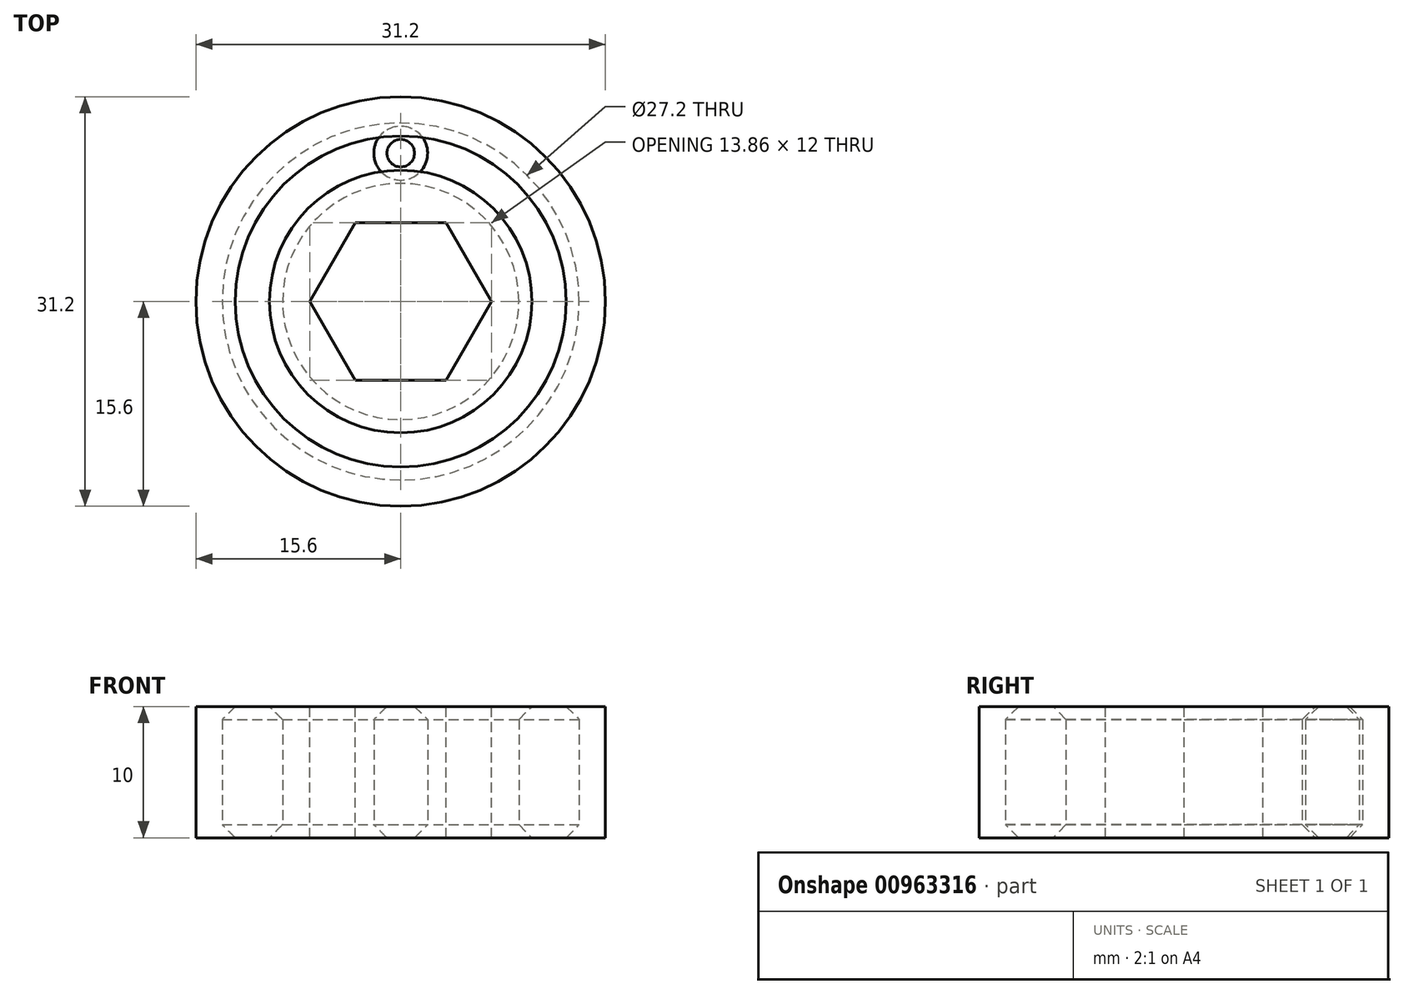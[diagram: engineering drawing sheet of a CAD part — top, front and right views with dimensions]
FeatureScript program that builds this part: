
annotation { "Feature Type Name" : "Feature", "Feature Type Description" : "" }
export const myFeature = defineFeature(function(context is Context, id is Id, definition is map)
    precondition{}
    {
        {
            var Q0;
            Q0=qCreatedBy(makeId("Right.planeOp"),FACE);
            var sketch = newSketch(context, id + "F0", { "sketchPlane" : qUnion([Q0])});
            skLineSegment(sketch, "E0", {"start": v(0, 0) * mm, "end": v(0, 10) * mm});
            skLineSegment(sketch, "E1", {"start": v(0, 0) * mm, "end": v(10, 0) * mm});
            skLineSegment(sketch, "E2", {"start": v(10, 0) * mm, "end": v(9, 1) * mm});
            skLineSegment(sketch, "E3", {"start": v(9, 1) * mm, "end": v(9, 9) * mm});
            skLineSegment(sketch, "E4", {"start": v(9, 9) * mm, "end": v(10, 10) * mm});
            skLineSegment(sketch, "E5", {"start": v(10, 10) * mm, "end": v(0, 10) * mm});
            skLineSegment(sketch, "E6", {"start": v(9.25, 1) * mm, "end": v(9.25, 9) * mm});
            skLineSegment(sketch, "E7", {"start": v(9.25, 9) * mm, "end": v(10.25, 10) * mm});
            skLineSegment(sketch, "E8", {"start": v(9.25, 1) * mm, "end": v(10.25, 0) * mm});
            skLineSegment(sketch, "E9", {"start": v(10.25, 10) * mm, "end": v(11.3, 10) * mm});
            skLineSegment(sketch, "E10", {"start": v(10.25, 0) * mm, "end": v(11.3, 0) * mm});
            skLineSegment(sketch, "E11", {"start": v(11.3, 0) * mm, "end": v(11.3, 10) * mm});
            skLineSegment(sketch, "E12.MirrorCS", {"start": v(13.35, 1) * mm, "end": v(13.35, 9) * mm});
            skLineSegment(sketch, "E13.MirrorCS", {"start": v(13.35, 9) * mm, "end": v(12.35, 10) * mm});
            skLineSegment(sketch, "E14.MirrorCS", {"start": v(13.35, 1) * mm, "end": v(12.35, 0) * mm});
            skLineSegment(sketch, "E15.MirrorCS", {"start": v(12.6, 10) * mm, "end": v(15.6, 10) * mm});
            skLineSegment(sketch, "E16.MirrorCS", {"start": v(13.6, 9) * mm, "end": v(12.6, 10) * mm});
            skLineSegment(sketch, "E17.MirrorCS", {"start": v(13.6, 1) * mm, "end": v(13.6, 9) * mm});
            skLineSegment(sketch, "E18.MirrorCS", {"start": v(12.6, 0) * mm, "end": v(13.6, 1) * mm});
            skLineSegment(sketch, "E19.MirrorCS", {"start": v(15.6, 0) * mm, "end": v(12.6, 0) * mm});
            skLineSegment(sketch, "E20", {"start": v(15.6, 10) * mm, "end": v(15.6, 0) * mm});
            skPoint(sketch, "E21.orphan", {"position": v(22.6, 10) * mm});
            skPoint(sketch, "E22.orphan", {"position": v(22.6, 0) * mm});
            skSolve(sketch);
        }
        {
            var Q0;
            Q0=makeQuery(id+"F0.imprint","IMPRINT",FACE,{"disambiguationData":[TD([[makeQuery(id+"F0.imprint","IMPRINT",EDGE,{"derivedFrom":sQuery(id+"F0.wireOp",EDGE,"E0")}),-1.0]])]});
            var Q1;
            Q1=sQuery(id+"F0.wireOp",EDGE,"E0");
            revolve(context, id + "F1", {"surfaceOperationType" : NewSurfaceOperationType.NEW, "entities" : qUnion([Q0]), "axis" : qUnion([Q1]), "revolveType" : RevolveType.FULL});
        }
        {
            var Q0;
            Q0=makeQuery(id+"F0.imprint","IMPRINT",FACE,{"disambiguationData":[TD([[makeQuery(id+"F0.imprint","IMPRINT",EDGE,{"derivedFrom":sQuery(id+"F0.wireOp",EDGE,"E6")}),-1.0]])]});
            var Q1;
            Q1=sQuery(id+"F0.wireOp",EDGE,"E11");
            revolve(context, id + "F2", {"surfaceOperationType" : NewSurfaceOperationType.NEW, "entities" : qUnion([Q0]), "axis" : qUnion([Q1]), "revolveType" : RevolveType.FULL});
        }
        {
            var Q0;
            Q0=makeQuery(id+"F0.imprint","IMPRINT",FACE,{"disambiguationData":[TD([[makeQuery(id+"F0.imprint","IMPRINT",EDGE,{"derivedFrom":sQuery(id+"F0.wireOp",EDGE,"E15.MirrorCS")}),-1.0]])]});
            var Q1;
            Q1=sQuery(id+"F0.wireOp",EDGE,"E0");
            revolve(context, id + "F3", {"surfaceOperationType" : NewSurfaceOperationType.NEW, "entities" : qUnion([Q0]), "axis" : qUnion([Q1]), "revolveType" : RevolveType.FULL});
        }
        {
            var Q0;
            Q0=makeQuery(id+"F1.opRevolve","SWEPT_FACE",FACE,{"disambiguationData":[OSD([sQuery(id+"F0.wireOp",EDGE,"E5")])]});
            var sketch = newSketch(context, id + "F4", { "sketchPlane" : qUnion([Q0])});
            skCircle(sketch, "E23.cCircle", {"center": v(0, 0) * mm, "radius": 6 * mm, "construction": true});
            skLineSegment(sketch, "E23.0", {"start": v(-3.46, 6) * mm, "end": v(3.46, 6) * mm});
            skLineSegment(sketch, "E23.1", {"start": v(3.46, 6) * mm, "end": v(6.93, 0) * mm});
            skLineSegment(sketch, "E23.2", {"start": v(6.93, 0) * mm, "end": v(3.46, -6) * mm});
            skLineSegment(sketch, "E23.3", {"start": v(3.46, -6) * mm, "end": v(-3.46, -6) * mm});
            skLineSegment(sketch, "E23.4", {"start": v(-3.46, -6) * mm, "end": v(-6.93, 0) * mm});
            skLineSegment(sketch, "E23.5", {"start": v(-6.93, 0) * mm, "end": v(-3.46, 6) * mm});
            skPoint(sketch, "E23.0.midPoint", {"position": v(0, 6) * mm});
            skSolve(sketch);
        }
        {
            var Q0;
            Q0 = qSketchRegion(id + "F4", true);
            extrude(context, id + "F5", {"entities" : qUnion([Q0]), "operationType" : NewBodyOperationType.REMOVE, "oppositeDirection" : true, "depth" : 25 * mm, "offsetDistance" : 25 * mm});
        }
    });
